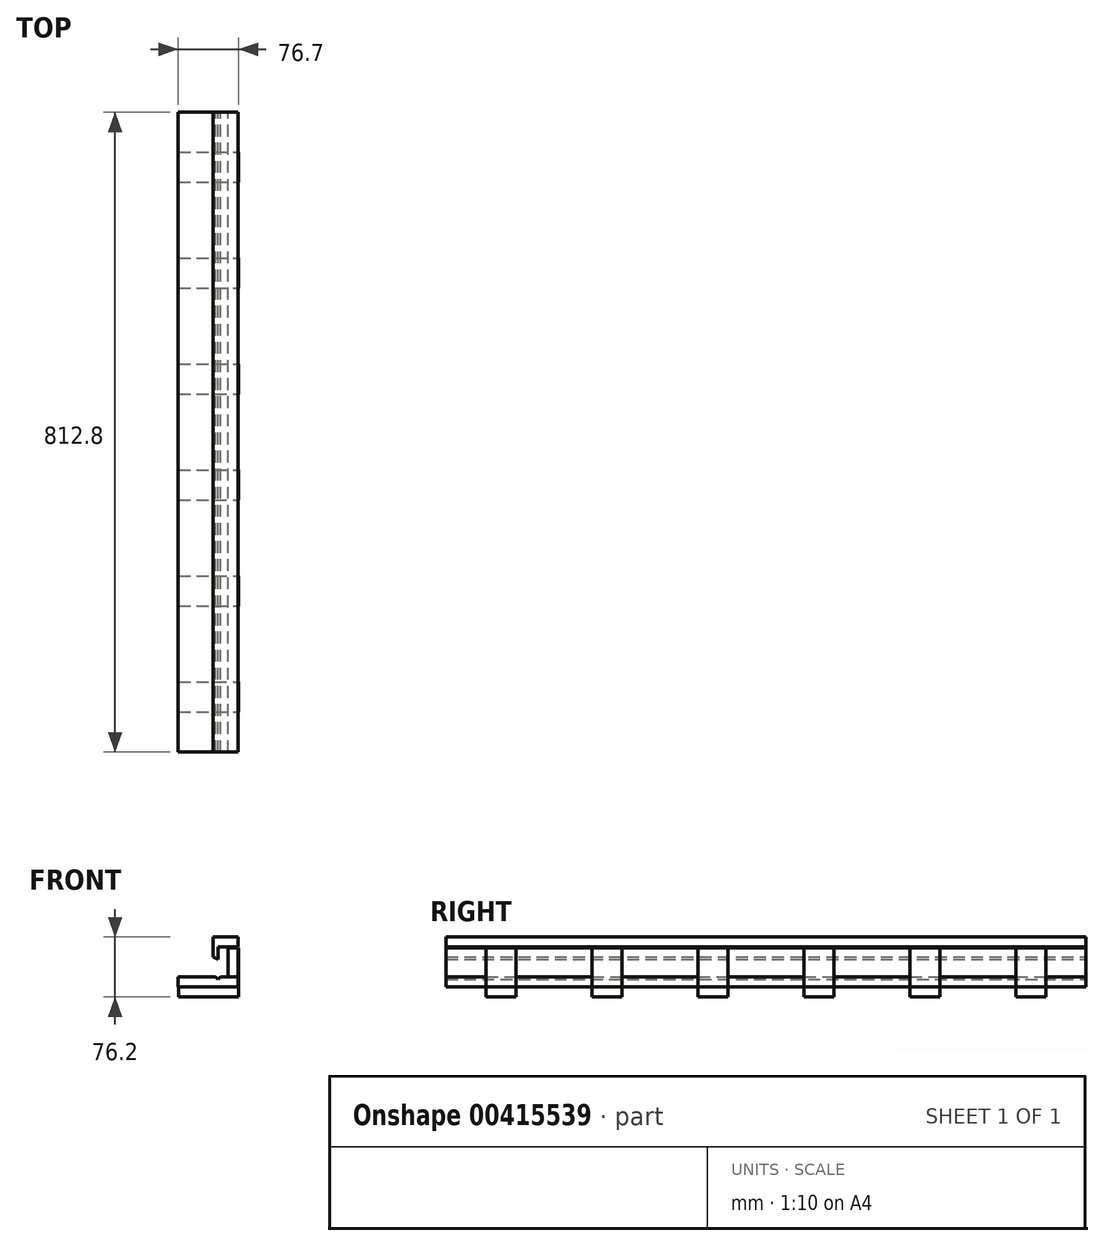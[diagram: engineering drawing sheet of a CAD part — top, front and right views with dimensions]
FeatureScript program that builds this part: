
annotation { "Feature Type Name" : "Feature", "Feature Type Description" : "" }
export const myFeature = defineFeature(function(context is Context, id is Id, definition is map)
    precondition{}
    {
        {
            assignVariable(context, id + "F0", {"name" : "trimD", "anyValue" : .5});
        }
        {
            var Q0;
            Q0=qCreatedBy(makeId("Front.planeOp"),FACE);
            var sketch = newSketch(context, id + "F1", { "sketchPlane" : qUnion([Q0])});
            skLineSegment(sketch, "E0.bottom", {"start": v(0, 0) * mm, "end": v(-12.7, 0) * mm});
            skLineSegment(sketch, "E0.top", {"start": v(0, 38.1) * mm, "end": v(-12.7, 38.1) * mm});
            skLineSegment(sketch, "E0.left", {"start": v(0, 0) * mm, "end": v(0, 38.1) * mm});
            skLineSegment(sketch, "E0.right", {"start": v(-12.7, 0) * mm, "end": v(-12.7, 38.1) * mm});
            skSolve(sketch);
        }
        {
            var Q0;
            Q0=qCreatedBy(makeId("Front.planeOp"),FACE);
            var sketch = newSketch(context, id + "F2", { "sketchPlane" : qUnion([Q0])});
            skLineSegment(sketch, "E1.bottom", {"start": v(-88.9, 0) * mm, "end": v(-12.7, 0) * mm});
            skLineSegment(sketch, "E1.top", {"start": v(-88.9, 19.05) * mm, "end": v(-12.7, 19.05) * mm});
            skLineSegment(sketch, "E1.left", {"start": v(-88.9, 0) * mm, "end": v(-88.9, 19.05) * mm});
            skLineSegment(sketch, "E1.right", {"start": v(-12.7, 0) * mm, "end": v(-12.7, 19.05) * mm});
            skSolve(sketch);
        }
        {
            var Q0;
            Q0=qCreatedBy(makeId("Front.planeOp"),FACE);
            var sketch = newSketch(context, id + "F3", { "sketchPlane" : qUnion([Q0])});
            skLineSegment(sketch, "E2.bottom", {"start": v(0, 0) * mm, "end": v(12.7, 0) * mm});
            skLineSegment(sketch, "E2.top", {"start": v(0, 36.83) * mm, "end": v(12.7, 36.83) * mm});
            skLineSegment(sketch, "E2.left", {"start": v(0, 0) * mm, "end": v(0, 36.83) * mm});
            skLineSegment(sketch, "E2.right", {"start": v(12.7, 0) * mm, "end": v(12.7, 36.83) * mm});
            skSolve(sketch);
        }
        {
            var Q0;
            Q0=qCreatedBy(makeId("Front.planeOp"),FACE);
            var sketch = newSketch(context, id + "F4", { "sketchPlane" : qUnion([Q0])});
            skLineSegment(sketch, "E3", {"start": v(12.7, 0) * mm, "end": v(12.7, -12.7) * mm});
            skLineSegment(sketch, "E4", {"start": v(12.7, -12.7) * mm, "end": v(-63.5, -12.7) * mm});
            skLineSegment(sketch, "E5", {"start": v(-63.5, -12.7) * mm, "end": v(-63.5, 0) * mm});
            skLineSegment(sketch, "E6", {"start": v(-63.5, 0) * mm, "end": v(-15.87, 0) * mm});
            skLineSegment(sketch, "E7", {"start": v(-15.87, 0) * mm, "end": v(-12.7, -3.17) * mm});
            skLineSegment(sketch, "E8", {"start": v(-12.7, -3.18) * mm, "end": v(-9.53, 0) * mm});
            skLineSegment(sketch, "E9", {"start": v(-9.53, 0) * mm, "end": v(12.7, 0) * mm});
            skSolve(sketch);
        }
        {
            var Q0;
            Q0=qCreatedBy(makeId("Front.planeOp"),FACE);
            var sketch = newSketch(context, id + "F5", { "sketchPlane" : qUnion([Q0])});
            skLineSegment(sketch, "E10.bottom", {"start": v(-12.7, 38.1) * mm, "end": v(12.7, 38.1) * mm});
            skLineSegment(sketch, "E10.top", {"start": v(-12.7, 50.8) * mm, "end": v(12.7, 50.8) * mm});
            skLineSegment(sketch, "E10.left", {"start": v(-12.7, 38.1) * mm, "end": v(-12.7, 50.8) * mm});
            skLineSegment(sketch, "E10.right", {"start": v(12.7, 38.1) * mm, "end": v(12.7, 50.8) * mm});
            skLineSegment(sketch, "E11", {"start": v(-12.7, 50.8) * mm, "end": v(-12.7, 22.23) * mm});
            skLineSegment(sketch, "E12", {"start": v(-12.7, 22.23) * mm, "end": v(-19.05, 25.9) * mm});
            skLineSegment(sketch, "E13", {"start": v(-19.05, 25.9) * mm, "end": v(-19.05, 50.8) * mm});
            skLineSegment(sketch, "E14", {"start": v(-19.05, 50.8) * mm, "end": v(-12.7, 50.8) * mm});
            skSolve(sketch);
        }
        {
            var Q0;
            Q0 = qSketchRegion(id + "F3", true);
            extrude(context, id + "F6", {"entities" : qUnion([Q0]), "endBound" : BoundingType.SYMMETRIC, "depth" : 812.8 * mm});
        }
        {
            var Q0;
            Q0=makeQuery(id+"F4.imprint","IMPRINT",FACE,{"disambiguationData":[TD([[makeQuery(id+"F4.imprint","IMPRINT",EDGE,{"derivedFrom":sQuery(id+"F4.wireOp",EDGE,"E3")}),-1.0]])]});
            extrude(context, id + "F7", {"entities" : qUnion([Q0]), "endBound" : BoundingType.SYMMETRIC, "depth" : 812.8 * mm});
        }
        {
            var Q0;
            Q0 = qSketchRegion(id + "F5", true);
            extrude(context, id + "F8", {"entities" : qUnion([Q0]), "endBound" : BoundingType.SYMMETRIC, "depth" : 812.8 * mm});
        }
        {
            var Q0;
            Q0=makeQuery(id+"F7.opExtrude","SWEPT_FACE",FACE,{"disambiguationData":[OSD([sQuery(id+"F4.wireOp",EDGE,"E3")])]});
            var sketch = newSketch(context, id + "F9", { "sketchPlane" : qUnion([Q0])});
            skLineSegment(sketch, "E15.bottom", {"start": v(-355.6, -12.7) * mm, "end": v(-317.5, -12.7) * mm});
            skLineSegment(sketch, "E15.top", {"start": v(-355.6, 36.83) * mm, "end": v(-317.5, 36.83) * mm});
            skLineSegment(sketch, "E15.left", {"start": v(-355.6, -12.7) * mm, "end": v(-355.6, 36.83) * mm});
            skLineSegment(sketch, "E15.right", {"start": v(-317.5, -12.7) * mm, "end": v(-317.5, 36.83) * mm});
            skLineSegment(sketch, "E16.1.0.0", {"start": v(-220.98, -12.7) * mm, "end": v(-182.88, -12.7) * mm});
            skLineSegment(sketch, "E16.1.0.1", {"start": v(-182.88, -12.7) * mm, "end": v(-182.88, 36.83) * mm});
            skLineSegment(sketch, "E16.1.0.2", {"start": v(-220.98, 36.83) * mm, "end": v(-182.88, 36.83) * mm});
            skLineSegment(sketch, "E16.1.0.3", {"start": v(-220.98, -12.7) * mm, "end": v(-220.98, 36.83) * mm});
            skLineSegment(sketch, "E16.2.0.0", {"start": v(-86.36, -12.7) * mm, "end": v(-48.26, -12.7) * mm});
            skLineSegment(sketch, "E16.2.0.1", {"start": v(-48.26, -12.7) * mm, "end": v(-48.26, 36.83) * mm});
            skLineSegment(sketch, "E16.2.0.2", {"start": v(-86.36, 36.83) * mm, "end": v(-48.26, 36.83) * mm});
            skLineSegment(sketch, "E16.2.0.3", {"start": v(-86.36, -12.7) * mm, "end": v(-86.36, 36.83) * mm});
            skLineSegment(sketch, "E16.direction1", {"start": v(-355.6, -12.7) * mm, "end": v(-220.98, -12.7) * mm, "construction": true});
            skLineSegment(sketch, "E17.0.3.0", {"start": v(48.26, -12.7) * mm, "end": v(86.36, -12.7) * mm});
            skLineSegment(sketch, "E17.3.3.0", {"start": v(86.36, -12.7) * mm, "end": v(86.36, 36.83) * mm});
            skLineSegment(sketch, "E17.6.3.0", {"start": v(48.26, 36.83) * mm, "end": v(86.36, 36.83) * mm});
            skLineSegment(sketch, "E17.9.3.0", {"start": v(48.26, -12.7) * mm, "end": v(48.26, 36.83) * mm});
            skLineSegment(sketch, "E17.0.4.0", {"start": v(182.88, -12.7) * mm, "end": v(220.98, -12.7) * mm});
            skLineSegment(sketch, "E17.3.4.0", {"start": v(220.98, -12.7) * mm, "end": v(220.98, 36.83) * mm});
            skLineSegment(sketch, "E17.6.4.0", {"start": v(182.88, 36.83) * mm, "end": v(220.98, 36.83) * mm});
            skLineSegment(sketch, "E17.9.4.0", {"start": v(182.88, -12.7) * mm, "end": v(182.88, 36.83) * mm});
            skLineSegment(sketch, "E18.0.5.0", {"start": v(317.5, -12.7) * mm, "end": v(355.6, -12.7) * mm});
            skLineSegment(sketch, "E18.3.5.0", {"start": v(355.6, -12.7) * mm, "end": v(355.6, 36.83) * mm});
            skLineSegment(sketch, "E18.6.5.0", {"start": v(317.5, 36.83) * mm, "end": v(355.6, 36.83) * mm});
            skLineSegment(sketch, "E18.9.5.0", {"start": v(317.5, -12.7) * mm, "end": v(317.5, 36.83) * mm});
            skSolve(sketch);
        }
        {
            var Q0;
            Q0 = qSketchRegion(id + "F9", true);
            extrude(context, id + "F10", {"entities" : qUnion([Q0]), "depth" : (getVariable(context, 'trimD')) * mm});
        }
        {
            var Q0;
            Q0=makeQuery(id+"F10.opExtrude","CAP_FACE",FACE,{"disambiguationData":[OSD([sQuery(id+"F9.wireOp",EDGE,"E15.bottom"),sQuery(id+"F9.wireOp",EDGE,"E15.top"),sQuery(id+"F9.wireOp",EDGE,"E15.left"),sQuery(id+"F9.wireOp",EDGE,"E15.right")])],"isStart":false});
            var sketch = newSketch(context, id + "F11", { "sketchPlane" : qUnion([Q0])});
            skLineSegment(sketch, "E19.bottom", {"start": v(-355.6, -25.4) * mm, "end": v(-317.5, -25.4) * mm});
            skLineSegment(sketch, "E19.top", {"start": v(-355.6, -12.7) * mm, "end": v(-317.5, -12.7) * mm});
            skLineSegment(sketch, "E19.left", {"start": v(-355.6, -25.4) * mm, "end": v(-355.6, -12.7) * mm});
            skLineSegment(sketch, "E19.right", {"start": v(-317.5, -25.4) * mm, "end": v(-317.5, -12.7) * mm});
            skLineSegment(sketch, "E20.1.0.0", {"start": v(-220.98, -25.4) * mm, "end": v(-182.88, -25.4) * mm});
            skLineSegment(sketch, "E20.1.0.1", {"start": v(-220.98, -25.4) * mm, "end": v(-220.98, -12.7) * mm});
            skLineSegment(sketch, "E20.1.0.2", {"start": v(-182.88, -25.4) * mm, "end": v(-182.88, -12.7) * mm});
            skLineSegment(sketch, "E20.1.0.3", {"start": v(-220.98, -12.7) * mm, "end": v(-182.88, -12.7) * mm});
            skLineSegment(sketch, "E20.2.0.0", {"start": v(-86.36, -25.4) * mm, "end": v(-48.26, -25.4) * mm});
            skLineSegment(sketch, "E20.2.0.1", {"start": v(-86.36, -25.4) * mm, "end": v(-86.36, -12.7) * mm});
            skLineSegment(sketch, "E20.2.0.2", {"start": v(-48.26, -25.4) * mm, "end": v(-48.26, -12.7) * mm});
            skLineSegment(sketch, "E20.2.0.3", {"start": v(-86.36, -12.7) * mm, "end": v(-48.26, -12.7) * mm});
            skLineSegment(sketch, "E20.3.0.0", {"start": v(48.26, -25.4) * mm, "end": v(86.36, -25.4) * mm});
            skLineSegment(sketch, "E20.3.0.1", {"start": v(48.26, -25.4) * mm, "end": v(48.26, -12.7) * mm});
            skLineSegment(sketch, "E20.3.0.2", {"start": v(86.36, -25.4) * mm, "end": v(86.36, -12.7) * mm});
            skLineSegment(sketch, "E20.3.0.3", {"start": v(48.26, -12.7) * mm, "end": v(86.36, -12.7) * mm});
            skLineSegment(sketch, "E20.4.0.0", {"start": v(182.88, -25.4) * mm, "end": v(220.98, -25.4) * mm});
            skLineSegment(sketch, "E20.4.0.1", {"start": v(182.88, -25.4) * mm, "end": v(182.88, -12.7) * mm});
            skLineSegment(sketch, "E20.4.0.2", {"start": v(220.98, -25.4) * mm, "end": v(220.98, -12.7) * mm});
            skLineSegment(sketch, "E20.4.0.3", {"start": v(182.88, -12.7) * mm, "end": v(220.98, -12.7) * mm});
            skLineSegment(sketch, "E20.5.0.0", {"start": v(317.5, -25.4) * mm, "end": v(355.6, -25.4) * mm});
            skLineSegment(sketch, "E20.5.0.1", {"start": v(317.5, -25.4) * mm, "end": v(317.5, -12.7) * mm});
            skLineSegment(sketch, "E20.5.0.2", {"start": v(355.6, -25.4) * mm, "end": v(355.6, -12.7) * mm});
            skLineSegment(sketch, "E20.5.0.3", {"start": v(317.5, -12.7) * mm, "end": v(355.6, -12.7) * mm});
            skLineSegment(sketch, "E20.direction1", {"start": v(-355.6, -25.4) * mm, "end": v(-220.98, -25.4) * mm, "construction": true});
            skSolve(sketch);
        }
        {
            var Q0;
            Q0 = qSketchRegion(id + "F11", true);
            extrude(context, id + "F12", {"entities" : qUnion([Q0]), "oppositeDirection" : true, "depth" : 76.2 * mm});
        }
    });
